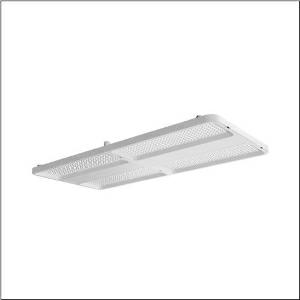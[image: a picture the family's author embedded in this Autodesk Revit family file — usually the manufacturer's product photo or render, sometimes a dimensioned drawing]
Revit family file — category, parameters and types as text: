
# Revit family: highbay_11_maxi_51hn12db4vda
name_source: partatom
category: Lighting Fixtures
units: mm (PartAtom-declared; Revit-internal decimal feet)

## family parameters
Cut with Voids When Loaded = No
Host = Face
Light Source = No
Part Type = Normal
Room Calculation Point = No
Round Connector Dimension = Use Diameter
Shared = No

## types (1)
- --- (1 x LED, 9070 lm, 44.6 W, 4000K)
    Apparent Load = 45 VA
    CIE Flux Codes = 87 98 100 100 100
    Color Rendering = 80
    Color Temperature = 4000K
    Default Elevation = 1800 mm
    Description = high bay luminaire Highbay 11 maxi; direct symmetric wide distribution, light control with lens of PMMA; UGR ≤ 22 (X = 4H | Y = 8H | S = 0.25H | reflection values 70/50/20); luminous flux: 56.000lm; light colour: 840, colour temperature: 4000K, MacAdam ≤ 2 SDCM (initial), colour rendering: CRI > 80; luminous efficacy: 189,9lm/W; rated service life: 100.000h (L95) at AT= 25°C; control: DALI 2; luminaire connection: terminal, 5-pole, max. 2.5mm² (cable entry for one cable, Ø 8.5..16mm); mains connection: 230..240V, AC/DC 0/50..60Hz; connected load: 294,9W; protection rating (complete): IP66; insulation class (complete): insulation class I (protective earthing); protection symbol: D; impact resistance: IK08; certification: CE, ENEC, VDE, UKCA; luminaire for central battery installations according to EN 60598-2-22, internal wiring halogen-free; luminaire Suitable for use in the food industry according to the specifications of IFS-Food, HACCP and/or BRC; LABS conformity tested according to VDMA 24364:2018-05; housing frame of high-performance plastic PA6, matt traffic white (RAL 9016); cover of PMMA; dimension (LxWxH): 946 x 442 x 72mm; permissible operating ambient temperature: -40..+50°C (reducing of maximum allowable ambient temperature of 5°C with ceiling mounting); packaging unit: 1 piece; (delivery without accessories; please order mounting accessories separately)
    Height = 72 mm  [stored 0.23622 ft]
    Lamp = 1 x LED
    Lamp Light Flux = 9070 lm
    Lamp Power = 44.6 W
    Lamp count = 1
    Length = 946 mm
    Luminous efficacy = 203 lm/W
    Manufacturer = Siteco
    ModVariant = No
    Model = 51HN12DB4VDA
    Mounting Place = Ceiling
    Mounting Type = Pendant
    Number of Poles = 1
    OnlyDefault = Yes
    Power Factor = 1
    Product Name = Highbay 11 maxi
    Product group = high bay luminaire
    ProductGroupID = 902
    Protection Class = Protection class I
    Protection Degree = IP 66
    RLX_Detail_Level = 1
    RLX_Emergency_Light_Flux = 0 lm
    RLX_Emergency_Type = 0
    RLX_Emergency_Type_DB = No
    RlxData = <blob elided: 127037 chars, md5=b40ed2f9>
    Socket = socket
    Standby Power = 0 W
    System Light Flux = 9070 lm
    System Power = 45 W
    Type Comments = : DC mode (central or group accumulator) initial emergency light level
    Type Image = l_1363244.jpg
    URL = http://relux.com
    VarID = @adj_024877
    Voltage = 0 V
    Weight = 0.00 kg
    Width = 442 mm

note: [stored X ft] marks values corroborated as IEEE doubles in the binary element streams (Revit-internal decimal feet)

## geometry (parser evidence)
native form markers: Blend x4, Sweep x10
no freeform markers — native parametric forms only
